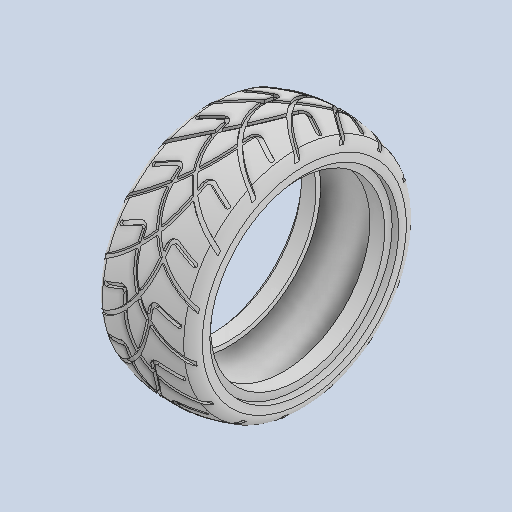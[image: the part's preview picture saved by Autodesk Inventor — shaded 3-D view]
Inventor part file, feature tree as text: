
AUTODESK INVENTOR PART (.ipt)
format: ipt  version: 2024 (Build 280153000, 153)  size: 2,061,824 bytes
history: native  units: in
note: dims shown in document units (in); Inventor stores cm internally (conversion verified against a paired STEP export)
features: sketch x4, revolve x2, other x2, fillet x1, plane x1, extrude x1, pattern_circular x1, mirror x1, direct_edit x1, projected_geometry x1
ambient origin geometry x8: Origin, YZ Plane, XZ Plane, XY Plane, X Axis, Y Axis, Z Axis, Center Point
bodies: Solid1 (feature_tree)
feature tree (15):
  revolve  "Revolution1"  [1 undecoded]
  fillet  "Fillet1"  Radius=0.23in
  plane  "Work Plane1"
  sketch  "Sketch3"  dims[d5=1.045in]
  extrude  "Extrusion1"  Depth=2.6in
  pattern_circular  "Circular Pattern1"  Angle=90.0deg  [1 undecoded]
  mirror  "Mirror1"
  direct_edit  "Direct Edit1"
  sketch  "Sketch1"  dims[d0=1.885in d1=0.07in d2=0.23in]
  sketch  "Sketch2"  dims[d3=2.045in d4=2.6in]
  other  "Srf1"
  sketch  "Sketch4"  dims[d6=0.05in d7=90.0deg d8=0.125in d9=0.0297in d10=90.0deg d11=1.375in d12=0.8744in d13=0.3268in d14=0.765in d15=0.2455in d16=0.0625in d17=0.1044in d18=0.0415in d19=0.1248in d20=0.2825in d21=1.0in d22=0.0in d23=5.9055in d24=360.0deg d26=3.937in d27=0.3937in d28=0.3937in]
  revolve  "RevolutionSrf1"  [1 undecoded]
  projected_geometry  "Project Cut Edges1"
  other  "Scale1"
note: 3 required parameter values undecoded (feature->parameter linkage not recoverable at this tier; creation-order binding heuristic only, values carry confidence <= 0.55)